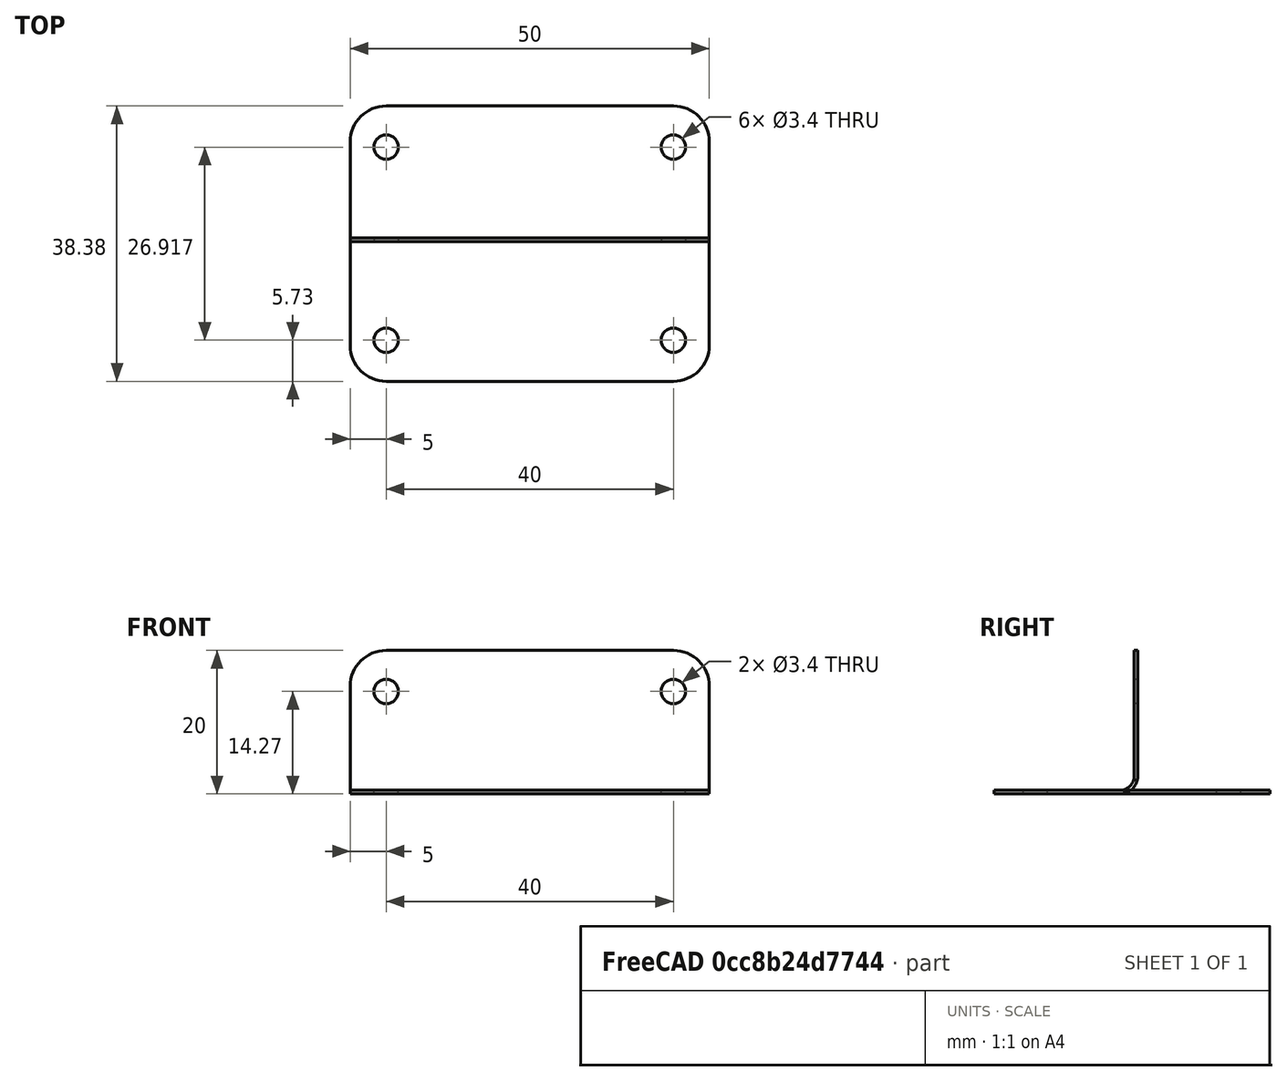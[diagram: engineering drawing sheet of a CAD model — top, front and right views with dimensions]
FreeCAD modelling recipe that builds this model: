
FCSTD DOCUMENT  (FreeCAD 0.21R31917 (Git))
Label: ugol90degX35mm
License: All rights reserved
LicenseURL: http://en.wikipedia.org/wiki/All_rights_reserved
objects: Sketcher::SketchObject×7, TechDraw::DrawViewDimension×5, PartDesign::SubShapeBinder×3, PartDesign::Hole×2, TechDraw::DrawViewPart×2, PartDesign::FeaturePython×1, PartDesign::Pocket×1, PartDesign::Mirrored×1, PartDesign::PolarPattern×1, PartDesign::MultiTransform×1, PartDesign::Body×1, Part::Feature×1, TechDraw::DrawSVGTemplate×1, TechDraw::DrawPage×1
note: 22 computed .brp shape members not serialized (recipe doc carries the construction recipe); baked Part::Feature solids carry a one-line shape summary decoded from their .brp

FEATURE [Sketcher::SketchObject] Sketch
  FullyConstrained = true
  MapMode = 5
  Placement = pos=(0,0,0) rot=(0.57735,0.57735,0.57735;2.0944rad)
  Support = -> [YZ_Plane]
  sketch-geometry (2):
    g0: LineSegment StartX=-20 StartY=0 StartZ=0 EndX=0 EndY=0 EndZ=0
    g1: LineSegment StartX=0 StartY=0 StartZ=0 EndX=0 EndY=20 EndZ=0
  constraints (6):
    c: PointOnObject(g0,g-1)
    c: Coincident(g0,g-1)
    c: Coincident(g0,g1)
    c: PointOnObject(g1,g-2)
    c: Equal(g1,g0)
    c: DistanceX(g0,g0) = 20  'length'
FEATURE [PartDesign::FeaturePython] BaseBend  # WARN: FeaturePython — macro-defined, semantics opaque (R4)
  BendSide = 1
  BendSketch = -> Sketch
  MidPlane = true
  Reverse = false
  length = 50
  radius = 2
  thickness = 0.5
FEATURE [Sketcher::SketchObject] Sketch001
  AttachmentOffset = pos=(0,-14.27,0) rot=(0,0,1;0rad)
  FullyConstrained = true
  MapMode = 5
  Placement = pos=(0,-14.27,0) rot=(0,0,1;0rad)
  Support = -> [XY_Plane]
  sketch-geometry (2):
    g0: Circle CenterX=20 CenterY=0 CenterZ=0 NormalX=0 NormalY=0 NormalZ=1 AngleXU=0 Radius=1.7
    g1: Circle CenterX=-20 CenterY=0 CenterZ=0 NormalX=0 NormalY=0 NormalZ=1 AngleXU=0 Radius=1.7
  constraints (5):
    c: PointOnObject(g0,g-1)
    c: Equal(g1,g0)
    c: Diameter(g1) = 3.4
    c: Symmetric(g0,g1,g-2)
    c: DistanceX(g1,g0) = 40
FEATURE [PartDesign::SubShapeBinder] Binder  label="hor"
  BindCopyOnChange = 0
  BindMode = 0
  ClaimChildren = false
  Context = -> Body [Binder.]
  Fuse = false
  MakeFace = true
  OffsetFill = false
  OffsetIntersection = false
  OffsetJoinType = 0
  OffsetOpenResult = false
  PartialLoad = false
  Relative = true
  Support = -> [Sketch001]
  _Version = 2
FEATURE [PartDesign::SubShapeBinder] Binder001
  BindCopyOnChange = 0
  BindMode = 0
  ClaimChildren = false
  Context = -> Body [Binder001.]
  Fuse = false
  MakeFace = true
  OffsetFill = false
  OffsetIntersection = false
  OffsetJoinType = 0
  OffsetOpenResult = false
  PartialLoad = false
  Placement = pos=(0,0,0) rot=(-1,0,0;1.5708rad)
  Relative = true
  Support = -> [Sketch001]
  _Version = 2
FEATURE [PartDesign::SubShapeBinder] Binder002  label="vert"
  BindCopyOnChange = 0
  BindMode = 0
  ClaimChildren = false
  Context = -> Body [Binder002.]
  Fuse = false
  MakeFace = true
  OffsetFill = false
  OffsetIntersection = false
  OffsetJoinType = 0
  OffsetOpenResult = false
  PartialLoad = false
  Relative = true
  Support = -> [Binder001]
  _Version = 2
FEATURE [PartDesign::Hole] Hole
  BaseFeature = -> BaseBend
  CustomThreadClearance = 0
  Depth = 25
  DepthType = 0
  Diameter = 3.4
  DrillForDepth = false
  DrillPoint = 1
  DrillPointAngle = 118
  HoleCutCountersinkAngle = 90
  HoleCutCustomValues = false
  HoleCutDepth = 0
  HoleCutDiameter = 6.1
  HoleCutType = 0
  ModelThread = false
  Profile = -> Binder
  Reversed = true
  Tapered = false
  TaperedAngle = 90
  ThreadClass = 0
  ThreadDepth = 25
  ThreadDepthType = 0
  ThreadDirection = 0
  ThreadFit = 0
  ThreadSize = 0
  ThreadType = 0
  Threaded = false
  UseCustomThreadClearance = false
FEATURE [PartDesign::Hole] Hole001
  BaseFeature = -> Hole
  CustomThreadClearance = 0
  Depth = 25
  DepthType = 0
  Diameter = 3.4
  DrillForDepth = false
  DrillPoint = 1
  DrillPointAngle = 118
  HoleCutCountersinkAngle = 90
  HoleCutCustomValues = false
  HoleCutDepth = 0
  HoleCutDiameter = 6.1
  HoleCutType = 0
  ModelThread = false
  Profile = -> Binder002
  Tapered = false
  TaperedAngle = 90
  ThreadClass = 0
  ThreadDepth = 25
  ThreadDepthType = 0
  ThreadDirection = 0
  ThreadFit = 0
  ThreadSize = 0
  ThreadType = 0
  Threaded = false
  UseCustomThreadClearance = false
FEATURE [Sketcher::SketchObject] Sketch002
  AttachmentOffset = pos=(25,-20,0) rot=(0,0,1;-1.5708rad)
  FullyConstrained = true
  MapMode = 5
  Placement = pos=(25,-20,0) rot=(0,0,1;4.71239rad)
  Support = -> [XY_Plane]
  expr: .AttachmentOffset.Base.x = BaseBend.length / 2
  expr: .AttachmentOffset.Base.y = -Sketch.Constraints.length
  sketch-geometry (3):
    g0: ArcOfCircle CenterX=-5 CenterY=-5 CenterZ=0 NormalX=0 NormalY=0 NormalZ=1 AngleXU=0 Radius=5 StartAngle=0 EndAngle=1.5708
    g1: LineSegment StartX=-1.6e-14 StartY=-5 StartZ=0 EndX=-1.6e-14 EndY=-1.6e-14 EndZ=0
    g2: LineSegment StartX=-1.6e-14 StartY=-1.6e-14 StartZ=0 EndX=-5 EndY=-1.6e-14 EndZ=0
  constraints (8):
    c: PointOnObject(g0,g-1)
    c: PointOnObject(g0,g-2)
    c: Coincident(g1,g2)
    c: Horizontal(g2)
    c: Vertical(g1)
    c: Tangent(g0,g1) = -1.5708
    c: Tangent(g2,g0) = -1.5708
    c: Diameter(g0) = 10
FEATURE [PartDesign::Pocket] Pocket
  BaseFeature = -> Hole001
  Direction = (0,0,-1)
  Length = 5
  Length2 = 5
  Midplane = true
  Profile = -> Sketch002
  ReferenceAxis = -> Sketch002 [N_Axis]
  Type = 1
FEATURE [PartDesign::Mirrored] Mirrored
  MirrorPlane = -> YZ_Plane
FEATURE [PartDesign::PolarPattern] PolarPattern
  Angle = 90
  Axis = -> X_Axis
  Occurrences = 2
  Reversed = true
FEATURE [PartDesign::MultiTransform] MultiTransform
  BaseFeature = -> Pocket
  Originals = -> [Pocket]
  Transformations = -> [Mirrored,PolarPattern]
FEATURE [PartDesign::Body] Body  label="Body_material_0.30ansi"
  Group = -> [Sketch,BaseBend,Sketch001,Binder,Binder001,Binder002,Hole,Hole001,Sketch002,Pocket,MultiTransform,Mirrored,PolarPattern]
  Origin = -> Origin
  Tip = -> MultiTransform
FEATURE [Part::Feature] Unfold
  shape: bbox 50 x 38.38 x 0.5 mm, 14 faces (baked)
FEATURE [Sketcher::SketchObject] Unfold_Sketch
  FullyConstrained = false
  sketch-geometry (12):
    g0: ArcOfCircle CenterX=-20 CenterY=13.3772 CenterZ=0 NormalX=0 NormalY=0 NormalZ=1 AngleXU=1.5708 Radius=5 StartAngle=0 EndAngle=1.5708
    g1: LineSegment StartX=-20 StartY=18.3772 StartZ=0 EndX=20 EndY=18.3772 EndZ=0
    g2: ArcOfCircle CenterX=20 CenterY=13.3772 CenterZ=0 NormalX=0 NormalY=0 NormalZ=1 AngleXU=1.5708 Radius=5 StartAngle=4.71239 EndAngle=6.28319
    g3: ArcOfCircle CenterX=20 CenterY=-15 CenterZ=0 NormalX=0 NormalY=0 NormalZ=1 AngleXU=-1.5708 Radius=5 StartAngle=2e-16 EndAngle=1.5708
    g4: LineSegment StartX=-20 StartY=-20 StartZ=0 EndX=20 EndY=-20 EndZ=0
    g5: ArcOfCircle CenterX=-20 CenterY=-15 CenterZ=0 NormalX=0 NormalY=0 NormalZ=1 AngleXU=-1.5708 Radius=5 StartAngle=4.71239 EndAngle=6.28319
    g6: Circle CenterX=20 CenterY=12.6472 CenterZ=0 NormalX=0 NormalY=0 NormalZ=1 AngleXU=-5e-16 Radius=1.7
    g7: Circle CenterX=-20 CenterY=12.6472 CenterZ=0 NormalX=0 NormalY=0 NormalZ=1 AngleXU=-5e-16 Radius=1.7
    g8: Circle CenterX=20 CenterY=-14.27 CenterZ=0 NormalX=0 NormalY=0 NormalZ=1 AngleXU=-3.14159 Radius=1.7
    g9: Circle CenterX=-20 CenterY=-14.27 CenterZ=0 NormalX=0 NormalY=0 NormalZ=1 AngleXU=-3.14159 Radius=1.7
    g10: LineSegment StartX=-25 StartY=-15 StartZ=0 EndX=-25 EndY=13.3772 EndZ=0
    g11: LineSegment StartX=25 StartY=-15 StartZ=0 EndX=25 EndY=13.3772 EndZ=0
FEATURE [Sketcher::SketchObject] Unfold_Sketch_Outline
  FullyConstrained = false
  sketch-geometry (8):
    g0: ArcOfCircle CenterX=-20 CenterY=13.3772 CenterZ=0 NormalX=0 NormalY=0 NormalZ=1 AngleXU=1.5708 Radius=5 StartAngle=0 EndAngle=1.5708
    g1: LineSegment StartX=-25 StartY=-15 StartZ=0 EndX=-25 EndY=13.3772 EndZ=0
    g2: ArcOfCircle CenterX=-20 CenterY=-15 CenterZ=0 NormalX=0 NormalY=0 NormalZ=1 AngleXU=-1.5708 Radius=5 StartAngle=4.71239 EndAngle=6.28319
    g3: LineSegment StartX=-20 StartY=-20 StartZ=0 EndX=20 EndY=-20 EndZ=0
    g4: ArcOfCircle CenterX=20 CenterY=-15 CenterZ=0 NormalX=0 NormalY=0 NormalZ=1 AngleXU=-1.5708 Radius=5 StartAngle=2e-16 EndAngle=1.5708
    g5: LineSegment StartX=25 StartY=-15 StartZ=0 EndX=25 EndY=13.3772 EndZ=0
    g6: ArcOfCircle CenterX=20 CenterY=13.3772 CenterZ=0 NormalX=0 NormalY=0 NormalZ=1 AngleXU=1.5708 Radius=5 StartAngle=4.71239 EndAngle=6.28319
    g7: LineSegment StartX=-20 StartY=18.3772 StartZ=0 EndX=20 EndY=18.3772 EndZ=0
FEATURE [Sketcher::SketchObject] Unfold_Sketch_Internal
  FullyConstrained = false
  sketch-geometry (4):
    g0: Circle CenterX=-20 CenterY=-14.27 CenterZ=0 NormalX=0 NormalY=0 NormalZ=1 AngleXU=-3.14159 Radius=1.7
    g1: Circle CenterX=20 CenterY=-14.27 CenterZ=0 NormalX=0 NormalY=0 NormalZ=1 AngleXU=-3.14159 Radius=1.7
    g2: Circle CenterX=-20 CenterY=12.6472 CenterZ=0 NormalX=0 NormalY=0 NormalZ=1 AngleXU=-5e-16 Radius=1.7
    g3: Circle CenterX=20 CenterY=12.6472 CenterZ=0 NormalX=0 NormalY=0 NormalZ=1 AngleXU=-5e-16 Radius=1.7
FEATURE [Sketcher::SketchObject] Unfold_Sketch_bends
  FullyConstrained = false
  Placement = pos=(0,-0.668281,0.309256) rot=(1,0,0;1.13738rad)
  sketch-geometry (1):
    g0: LineSegment StartX=25 StartY=-0.340765 StartZ=0 EndX=-25 EndY=-0.340765 EndZ=0
FEATURE [TechDraw::DrawSVGTemplate] Template
  Height = 210
  Orientation = 1
  Template = <path>
  Width = 297
FEATURE [TechDraw::DrawViewPart] View
  CoarseView = false
  Direction = (1,0,0)
  Focus = 100
  HardHidden = false
  IsoCount = 0
  IsoHidden = false
  IsoVisible = false
  LockPosition = false
  Perspective = false
  Rotation = 0
  ScaleType = 0
  SeamHidden = false
  SeamVisible = true
  SmoothHidden = false
  SmoothVisible = true
  Source = -> [Body]
  X = 183.386
  XDirection = (0,1,-1.19209e-07)
  Y = 124.769
FEATURE [TechDraw::DrawViewDimension] Dimension
  AngleOverride = false
  Arbitrary = false
  ArbitraryTolerances = false
  EqualTolerance = true
  ExtensionAngle = 0
  FormatSpec = R%.2w
  FormatSpecOverTolerance = %+.2w
  FormatSpecUnderTolerance = %+.2w
  Inverted = false
  LineAngle = 0
  LockPosition = false
  MeasureType = 1
  OverTolerance = 0
  References2D = -> [View]
  Rotation = 0
  ScaleType = 0
  TheoreticalExact = false
  Type = 4
  UnderTolerance = 0
  X = 0
  Y = 0
FEATURE [TechDraw::DrawViewDimension] Dimension001
  AngleOverride = false
  Arbitrary = false
  ArbitraryTolerances = false
  EqualTolerance = true
  ExtensionAngle = 0
  FormatSpec = %.2w
  FormatSpecOverTolerance = %+.2w
  FormatSpecUnderTolerance = %+.2w
  Inverted = false
  LineAngle = 0
  LockPosition = false
  MeasureType = 1
  OverTolerance = 0
  References2D = -> [View]
  Rotation = 0
  ScaleType = 0
  TheoreticalExact = false
  Type = 1
  UnderTolerance = 0
  X = 1.63707
  Y = -27.1226
FEATURE [TechDraw::DrawViewDimension] Dimension002
  AngleOverride = false
  Arbitrary = false
  ArbitraryTolerances = false
  EqualTolerance = true
  ExtensionAngle = 0
  FormatSpec = %.2w
  FormatSpecOverTolerance = %+.2w
  FormatSpecUnderTolerance = %+.2w
  Inverted = false
  LineAngle = 0
  LockPosition = false
  MeasureType = 1
  OverTolerance = 0
  References2D = -> [View]
  Rotation = 0
  ScaleType = 0
  TheoreticalExact = false
  Type = 2
  UnderTolerance = 0
  X = 24.9024
  Y = 2.06345
FEATURE [TechDraw::DrawViewPart] View001
  CoarseView = false
  Direction = (0,-1,0)
  Focus = 100
  HardHidden = false
  IsoCount = 0
  IsoHidden = false
  IsoVisible = false
  LockPosition = false
  Perspective = false
  Rotation = 0
  ScaleType = 0
  SeamHidden = false
  SeamVisible = true
  SmoothHidden = false
  SmoothVisible = true
  Source = -> [Body]
  X = 122.601
  XDirection = (1,0,0)
  Y = 122.251
FEATURE [TechDraw::DrawViewDimension] Dimension003
  AngleOverride = false
  Arbitrary = false
  ArbitraryTolerances = false
  EqualTolerance = true
  ExtensionAngle = 0
  FormatSpec = %.2w
  FormatSpecOverTolerance = %+.2w
  FormatSpecUnderTolerance = %+.2w
  Inverted = false
  LineAngle = 0
  LockPosition = false
  MeasureType = 1
  OverTolerance = 0
  References2D = -> [View001]
  Rotation = 0
  ScaleType = 0
  TheoreticalExact = false
  Type = 1
  UnderTolerance = 0
  X = -0.972347
  Y = -23.7406
FEATURE [TechDraw::DrawViewDimension] Dimension004
  AngleOverride = false
  Arbitrary = false
  ArbitraryTolerances = false
  EqualTolerance = true
  ExtensionAngle = 0
  FormatSpec = %.2w
  FormatSpecOverTolerance = %+.2w
  FormatSpecUnderTolerance = %+.2w
  Inverted = false
  LineAngle = 0
  LockPosition = false
  MeasureType = 1
  OverTolerance = 0
  References2D = -> [View001]
  Rotation = 0
  ScaleType = 0
  TheoreticalExact = false
  Type = 1
  UnderTolerance = 0
  X = -1.82047
  Y = 17.3557
FEATURE [TechDraw::DrawPage] Page
  KeepUpdated = true
  NextBalloonIndex = 1
  ProjectionType = 0
  Template = -> Template
  Views = -> [View,Dimension,Dimension001,Dimension002,View001,Dimension003,Dimension004]
note: 1 file-system path scrubbed to <path> (originals preserved in the JSON sidecar)
